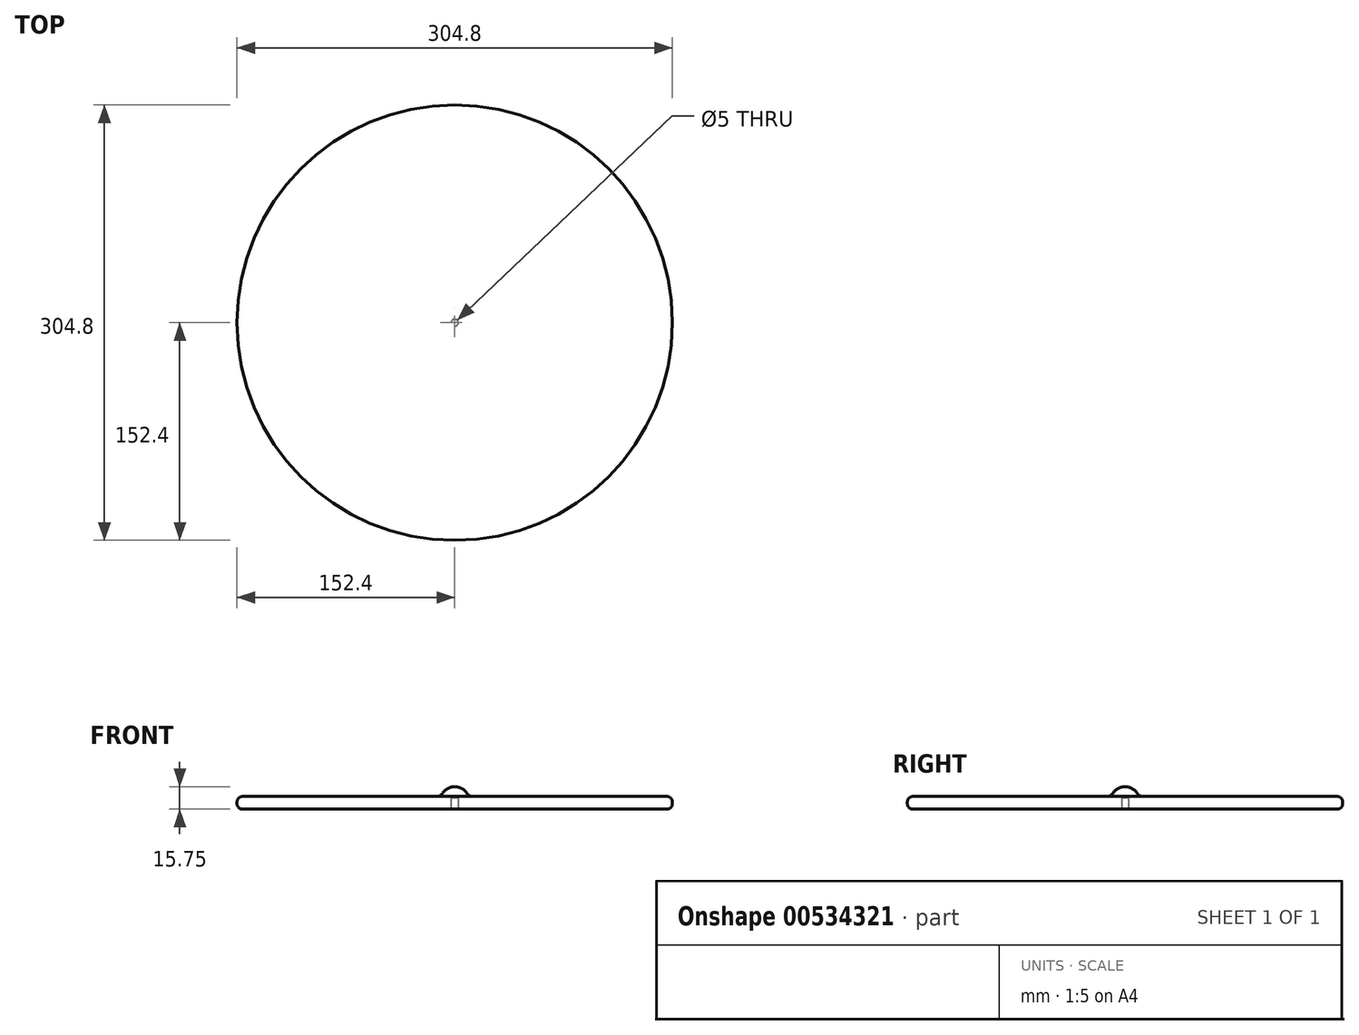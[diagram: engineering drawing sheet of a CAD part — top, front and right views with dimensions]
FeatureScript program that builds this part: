
annotation { "Feature Type Name" : "Feature", "Feature Type Description" : "" }
export const myFeature = defineFeature(function(context is Context, id is Id, definition is map)
    precondition{}
    {
        {
            var Q0;
            Q0=qCreatedBy(makeId("Front.planeOp"),FACE);
            var sketch = newSketch(context, id + "F0", { "sketchPlane" : qUnion([Q0])});
            skLineSegment(sketch, "E0", {"start": v(0, 0) * mm, "end": v(152.4, 0) * mm});
            skLineSegment(sketch, "E1", {"start": v(152.4, 0) * mm, "end": v(152.4, 8.9) * mm});
            skLineSegment(sketch, "E2", {"start": v(152.4, 8.9) * mm, "end": v(9.65, 8.9) * mm});
            skLineSegment(sketch, "E3", {"start": v(0, 15.75) * mm, "end": v(-3.82, 15.75) * mm});
            skArc(sketch, "E4", {"start": v(0, 15.75) * mm, "mid": v(5.92, 13.86) * mm, "end": v(9.65, 8.89) * mm});
            skLineSegment(sketch, "E5", {"start": v(0, 15.75) * mm, "end": v(0, 0) * mm});
            skSolve(sketch);
        }
        {
            var Q0;
            Q0=makeQuery(id+"F0.imprint","IMPRINT",FACE,{"disambiguationData":[TD([[makeQuery(id+"F0.imprint","IMPRINT",EDGE,{"derivedFrom":sQuery(id+"F0.wireOp",EDGE,"E0")}),1.0]])]});
            var Q1;
            Q1=sQuery(id+"F0.wireOp",EDGE,"E5");
            revolve(context, id + "F1", {"entities" : qUnion([Q0]), "axis" : qUnion([Q1]), "revolveType" : RevolveType.FULL});
        }
        {
            var Q0;
            Q0=makeQuery(id+"F1.opRevolve","SWEPT_EDGE",EDGE,{"disambiguationData":[OSD([sQuery(id+"F0.wireOp",EDGE,"E1"),sQuery(id+"F0.wireOp",EDGE,"E2")])]});
            fillet(context, id + "F2", {"entities" : qUnion([Q0]), "radius" : 3.8 * mm, "tangentPropagation" : true, "allowEdgeOverflow" : false});
        }
        {
            var Q0;
            Q0=makeQuery(id+"F1.opRevolve","SWEPT_EDGE",EDGE,{"disambiguationData":[OSD([sQuery(id+"F0.wireOp",EDGE,"E0"),sQuery(id+"F0.wireOp",EDGE,"E1")])]});
            fillet(context, id + "F3", {"entities" : qUnion([Q0]), "radius" : 3.8 * mm, "tangentPropagation" : true, "allowEdgeOverflow" : false});
        }
        {
            var Q0;
            Q0=makeQuery(id+"F1.opRevolve","SWEPT_EDGE",EDGE,{"disambiguationData":[OSD([sQuery(id+"F0.wireOp",EDGE,"E2"),sQuery(id+"F0.wireOp",EDGE,"E4")])]});
            fillet(context, id + "F4", {"entities" : qUnion([Q0]), "radius" : 5.08 * mm, "tangentPropagation" : true, "allowEdgeOverflow" : false});
        }
        {
            var Q0;
            Q0=makeQuery(id+"F1.opRevolve","SWEPT_FACE",FACE,{"disambiguationData":[OSD([sQuery(id+"F0.wireOp",EDGE,"E0")])]});
            var sketch = newSketch(context, id + "F5", { "sketchPlane" : qUnion([Q0])});
            skPoint(sketch, "E6", {"position": v(0, 0) * mm});
            skSolve(sketch);
        }
        {
            var Q0;
            Q0=sQuery(id+"F5.wireOp",VERTEX,"E6");
            var Q1;
            Q1=makeQuery(id+"F1.opRevolve","SWEPT_BODY",BODY,{"disambiguationData":[OSD([sQuery(id+"F0.wireOp",EDGE,"E0"),sQuery(id+"F0.wireOp",EDGE,"E1"),sQuery(id+"F0.wireOp",EDGE,"E2"),sQuery(id+"F0.wireOp",EDGE,"E4"),sQuery(id+"F0.wireOp",EDGE,"E5")])]});
            hole(context, id + "F6", {"style" : HoleStyle.SIMPLE, "endStyle" : HoleEndStyle.BLIND, "holeDiameter" : 5 * mm, "holeDepth" : 8 * mm, "tappedDepth" : 7.85 * mm, "tapClearance" : 6, "locations" : qUnion([Q0]), "scope" : qUnion([Q1])});
        }
    });
